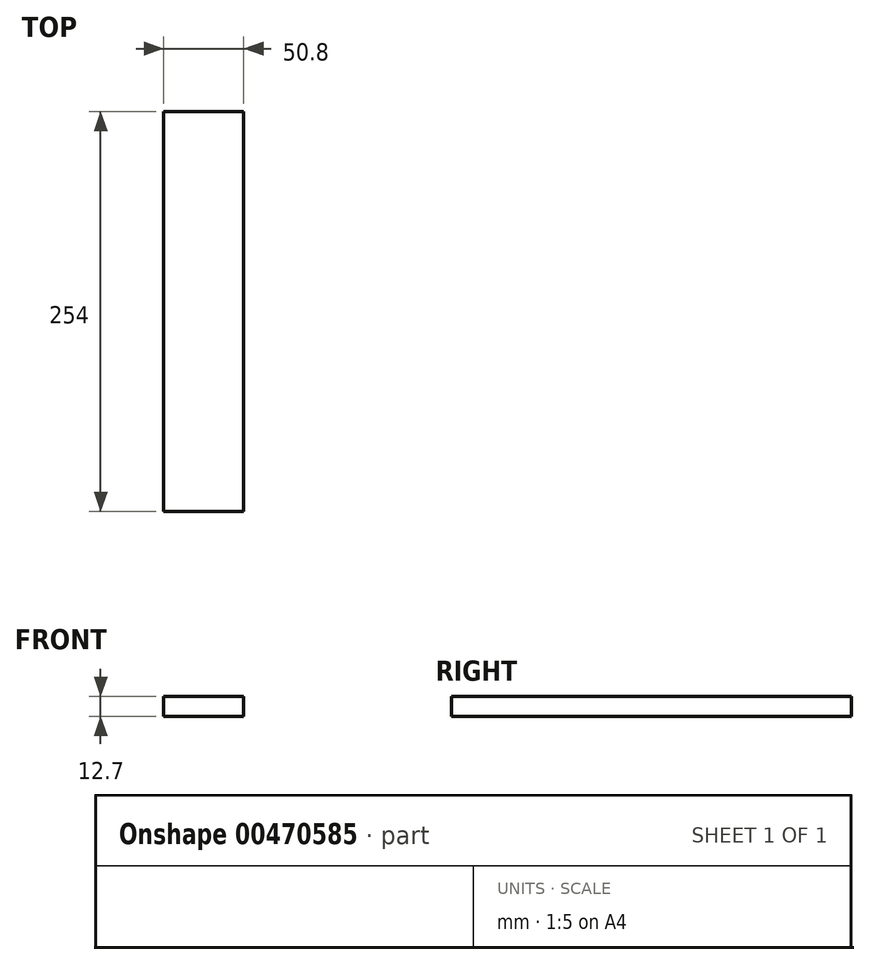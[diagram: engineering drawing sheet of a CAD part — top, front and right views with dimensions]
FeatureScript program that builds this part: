
annotation { "Feature Type Name" : "Feature", "Feature Type Description" : "" }
export const myFeature = defineFeature(function(context is Context, id is Id, definition is map)
    precondition{}
    {
        {
            var Q0;
            Q0=qCreatedBy(makeId("Top.planeOp"),FACE);
            var sketch = newSketch(context, id + "F0", { "sketchPlane" : qUnion([Q0])});
            skLineSegment(sketch, "E0.bottom", {"start": v(28.75, -127) * mm, "end": v(-22.05, -127) * mm});
            skLineSegment(sketch, "E0.top", {"start": v(28.75, 127) * mm, "end": v(-22.05, 127) * mm});
            skLineSegment(sketch, "E0.left", {"start": v(28.75, -127) * mm, "end": v(28.75, 127) * mm});
            skLineSegment(sketch, "E0.right", {"start": v(-22.05, -127) * mm, "end": v(-22.05, 127) * mm});
            skPoint(sketch, "E0.middle", {"position": v(3.35, 0) * mm});
            skSolve(sketch);
        }
        {
            var Q0;
            Q0=qSketchRegion(id+"F0",true);
            extrude(context, id + "F1", {"entities" : qUnion([Q0]), "depth" : 12.7 * mm});
        }
    });
